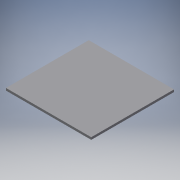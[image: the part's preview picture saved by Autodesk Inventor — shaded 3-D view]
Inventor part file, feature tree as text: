
AUTODESK INVENTOR PART (.ipt)
format: ipt  version: 2018.2 (Build 222227000, 227)  size: 89,600 bytes
history: native  units: in
note: dims shown in document units (in); Inventor stores cm internally (conversion verified against a paired STEP export)
features: extrude x1, sketch x1
ambient origin geometry x8: Origin, YZ Plane, XZ Plane, XY Plane, X Axis, Y Axis, Z Axis, Center Point
bodies: Solid1 (feature_tree)
feature tree (2):
  extrude  "Extrusion1"  Depth=0.75in
  sketch  "Sketch1"  dims[d0=28.226in d1=0.75in d2=27.398in d3=0.0in]
